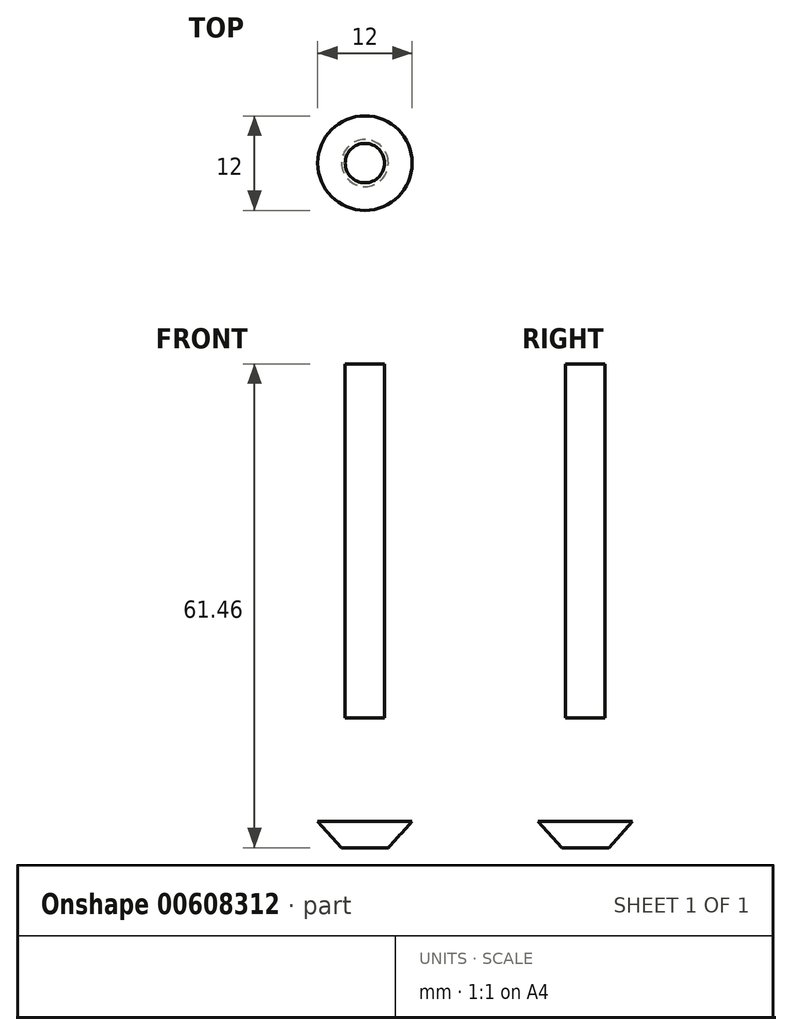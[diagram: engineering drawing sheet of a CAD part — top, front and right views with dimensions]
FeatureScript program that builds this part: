
annotation { "Feature Type Name" : "Feature", "Feature Type Description" : "" }
export const myFeature = defineFeature(function(context is Context, id is Id, definition is map)
    precondition{}
    {
        {
            var Q0;
            Q0=qCreatedBy(makeId("Front.planeOp"),FACE);
            var sketch = newSketch(context, id + "F0", { "sketchPlane" : qUnion([Q0])});
            skLineSegment(sketch, "E0", {"start": v(0, 80.2) * mm, "end": v(0, -104.53) * mm, "construction": true});
            skLineSegment(sketch, "E1", {"start": v(9, 3.33) * mm, "end": v(9, 22.46) * mm});
            skLineSegment(sketch, "E2", {"start": v(9, 22.46) * mm, "end": v(12.5, 22.46) * mm});
            skLineSegment(sketch, "E3", {"start": v(12.5, 22.46) * mm, "end": v(12.5, 71.46) * mm});
            skLineSegment(sketch, "E4", {"start": v(0, 57.18) * mm, "end": v(0, 5.22) * mm});
            skLineSegment(sketch, "E5", {"start": v(9, 3.33) * mm, "end": v(6, 3.33) * mm});
            skLineSegment(sketch, "E6", {"start": v(6, 3.33) * mm, "end": v(6, 61.46) * mm});
            skLineSegment(sketch, "E7", {"start": v(6, 61.46) * mm, "end": v(8, 61.46) * mm});
            skLineSegment(sketch, "E8", {"start": v(8, 61.46) * mm, "end": v(8, 71.46) * mm});
            skLineSegment(sketch, "E9", {"start": v(8, 71.46) * mm, "end": v(12.5, 71.46) * mm});
            skLineSegment(sketch, "E10.bottom", {"start": v(6, 61.46) * mm, "end": v(0, 61.46) * mm});
            skLineSegment(sketch, "E10.top", {"start": v(6, 3.33) * mm, "end": v(0, 3.33) * mm});
            skLineSegment(sketch, "E10.left", {"start": v(6, 61.46) * mm, "end": v(6, 3.33) * mm});
            skLineSegment(sketch, "E10.right", {"start": v(0, 61.46) * mm, "end": v(0, 3.33) * mm});
            skLineSegment(sketch, "E11", {"start": v(6, 3.33) * mm, "end": v(2.98, 0) * mm});
            skLineSegment(sketch, "E12", {"start": v(2.98, 0) * mm, "end": v(0, 0) * mm});
            skLineSegment(sketch, "E13", {"start": v(0, 0) * mm, "end": v(0, 3.33) * mm});
            skLineSegment(sketch, "E14.bottom", {"start": v(0, 61.46) * mm, "end": v(2.5, 61.46) * mm});
            skLineSegment(sketch, "E14.top", {"start": v(0, 16.46) * mm, "end": v(2.5, 16.46) * mm});
            skLineSegment(sketch, "E14.left", {"start": v(0, 61.46) * mm, "end": v(0, 16.46) * mm});
            skLineSegment(sketch, "E14.right", {"start": v(2.5, 61.46) * mm, "end": v(2.5, 16.46) * mm});
            skSolve(sketch);
        }
        {
            var Q0;
            Q0=makeQuery(id+"F0.imprint","IMPRINT",FACE,{"disambiguationData":[TD([[makeQuery(id+"F0.imprint","IMPRINT",EDGE,{"derivedFrom":sQuery(id+"F0.wireOp",EDGE,"E10.bottom")}),1.0]])]});
            var Q1;
            Q1=makeQuery(id+"F0.imprint","IMPRINT",FACE,{"disambiguationData":[TD([[makeQuery(id+"F0.imprint","IMPRINT",EDGE,{"derivedFrom":sQuery(id+"F0.wireOp",EDGE,"E10.top")}),1.0]])]});
            var Q2;
            Q2=sQuery(id+"F0.wireOp",EDGE,"E0");
            revolve(context, id + "F1", {"entities" : qUnion([Q0, Q1]), "axis" : qUnion([Q2]), "revolveType" : RevolveType.FULL});
        }
        {
            var Q0;
            Q0=qCreatedBy(makeId("Front.planeOp"),FACE);
            cPlane(context, id + "F2", {"entities" : qUnion([Q0]), "cplaneType" : CPlaneType.OFFSET, "offset" : 6 * mm, "width" : 150 * mm, "height" : 150 * mm});
        }
        {
            var Q0;
            Q0=qCreatedBy(id+"F2.planeOp",FACE);
            var sketch = newSketch(context, id + "F3", { "sketchPlane" : qUnion([Q0])});
            skPoint(sketch, "E15", {"position": v(0, 13.73) * mm});
            skLineSegment(sketch, "E16.bottom", {"start": v(-1.5, 13.73) * mm, "end": v(1.5, 13.73) * mm});
            skLineSegment(sketch, "E16.top", {"start": v(-1.5, 64.82) * mm, "end": v(1.5, 64.82) * mm});
            skLineSegment(sketch, "E16.left", {"start": v(-1.5, 13.73) * mm, "end": v(-1.5, 64.82) * mm});
            skLineSegment(sketch, "E16.right", {"start": v(1.5, 13.73) * mm, "end": v(1.5, 64.82) * mm});
            skArc(sketch, "E17", {"start": v(-1.5, 13.73) * mm, "mid": v(0, 12.23) * mm, "end": v(1.5, 13.73) * mm});
            skSolve(sketch);
        }
        {
            var Q0;
            Q0=makeQuery(id+"F3.imprint","IMPRINT",FACE,{"disambiguationData":[TD([[makeQuery(id+"F3.imprint","IMPRINT",EDGE,{"derivedFrom":sQuery(id+"F3.wireOp",EDGE,"E16.bottom")}),1.0]])]});
            var Q1;
            Q1=makeQuery(id+"F3.imprint","IMPRINT",FACE,{"disambiguationData":[TD([[makeQuery(id+"F3.imprint","IMPRINT",EDGE,{"derivedFrom":sQuery(id+"F3.wireOp",EDGE,"E16.bottom")}),-1.0]])]});
            extrude(context, id + "F4", {"entities" : qUnion([Q0, Q1]), "operationType" : NewBodyOperationType.REMOVE, "oppositeDirection" : true, "depth" : 2 * mm, "offsetDistance" : 25 * mm});
        }
    });
